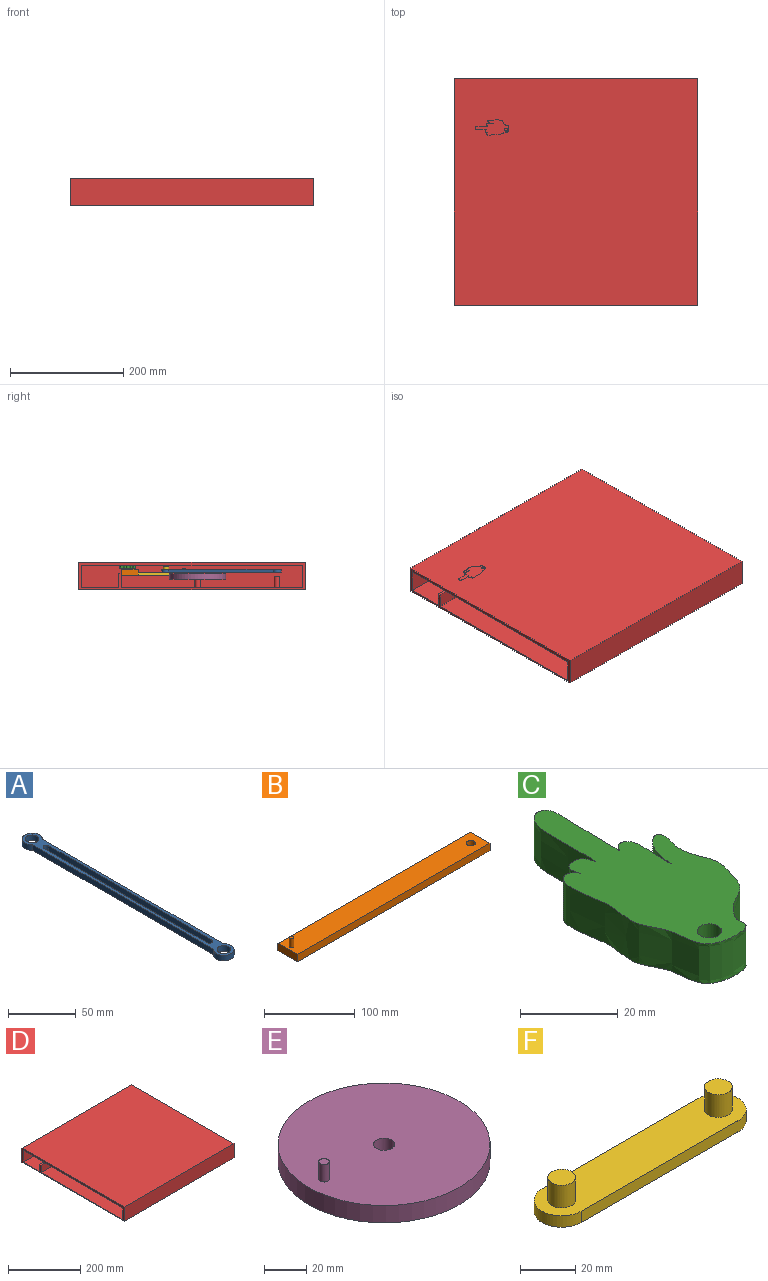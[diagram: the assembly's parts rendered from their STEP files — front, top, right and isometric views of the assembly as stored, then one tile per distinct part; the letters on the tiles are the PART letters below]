
ASSEMBLY  parts=6 mates=8
PART A: 12 faces, bbox 15x215x5 mm
  f0: plane 188.82x5mm, normal (1,0,0), area 944.1mm2, adj f1,f9,f10,f11
  f1: cylinder r=7.5mm len=15mm, axis (0,0,-1), area 180.9mm2, adj f0,f2,f10,f11
  f2: plane 188.82x5mm, normal (-1,0,0), area 944.1mm2, adj f1,f9,f10,f11
  f3: plane 170x5mm, normal (1,0,0), area 850mm2, adj f4,f6,f10,f11
  f4: cylinder r=2.5mm len=5mm, axis (0,0,-1), area 39.3mm2, adj f3,f5,f10,f11
  f5: plane 170x5mm, normal (-1,0,0), area 850mm2, adj f4,f6,f10,f11
  f6: cylinder r=2.5mm len=5mm, axis (0,0,-1), area 39.3mm2, adj f3,f5,f10,f11
  f7: cylinder r=5mm len=10mm, axis (0,0,-1), area 157.1mm2, adj f10,f11
  f8: cylinder r=5mm len=10mm, axis (0,0,-1), area 157.1mm2, adj f10,f11
  f9: cylinder r=7.5mm len=15mm, axis (0,0,-1), area 180.9mm2, adj f0,f2,f10,f11
  f10: plane 215x15mm, normal (0,0,1), area 1188.7mm2, adj f0,f1,f2,f3,f4,f5,f6,f7
  f11: plane 215x15mm, normal (0,0,-1), area 1188.7mm2, adj f0,f1,f2,f3,f4,f5,f6,f7
PART B: 9 faces, bbox 300x30x22.4 mm
  f0: plane 300x10mm, normal (0,1,0), area 3000mm2, adj f1,f4,f5,f6
  f1: plane 30x10mm, normal (-1,0,0), area 300mm2, adj f0,f2,f5,f6
  f2: plane 300x10mm, normal (0,-1,0), area 3000mm2, adj f1,f4,f5,f6
  f3: cylinder r=5mm len=10mm, axis (0,0,-1), area 314.2mm2, adj f5,f6
  f4: plane 30x10mm, normal (1,0,0), area 300mm2, adj f0,f2,f5,f6
  f5: plane 300x30mm, normal (0,0,1), area 8901.8mm2, adj f0,f1,f2,f3,f4,f7
  f6: plane 300x30mm, normal (0,0,-1), area 8921.5mm2, adj f0,f1,f2,f3,f4
  f7: cylinder r=2.5mm len=12.4mm, axis (0,0,-1), area 194.8mm2, adj f5,f8
  f8: plane 5x5mm, normal (0,0,1), area 19.6mm2, adj f7
PART C: 4 faces, bbox 28.3x60.6x10 mm
  f0: extruded ~58.81x27.04mm, area 1895.4mm2, adj f1,f2
  f1: plane 60.61x28.31mm, normal (0,0,1), area 962.1mm2, adj f0,f3
  f2: plane 60.61x28.31mm, normal (0,0,-1), area 962.1mm2, adj f0,f3
  f3: cylinder r=2.5mm len=10mm, axis (0,0,1), area 157.1mm2, adj f1,f2
PART D: 19 faces, bbox 430x400x48 mm
  f0: plane 425x390mm, normal (0,0,1), area 164592.9mm2, adj f2,f6,f8,f10,f11,f12,f14,f15
  f1: plane 430x48mm, normal (0,1,0), area 20640mm2, adj f2,f4,f5,f18
  f2: plane 400x48mm, normal (-1,0,0), area 3725mm2, adj f0,f1,f3,f5,f10,f11,f13,f14
  f3: plane 430x48mm, normal (0,-1,0), area 20640mm2, adj f2,f4,f5,f18
  f4: plane 400x48mm, normal (1,0,0), area 19200mm2, adj f1,f3,f5,f18
  f5: plane 430x400mm, normal (0,0,-1), area 172000mm2, adj f1,f2,f3,f4
  f6: cylinder r=5mm len=20mm, axis (0,0,-1), area 628.3mm2, adj f0,f7
  f7: plane 10x10mm, normal (0,0,1), area 78.5mm2, adj f6
  f8: cylinder r=5mm len=20mm, axis (0,0,-1), area 628.3mm2, adj f0,f9
  f9: plane 10x10mm, normal (0,0,1), area 78.5mm2, adj f8
  f10: plane 200x25mm, normal (0,1,0), area 5000mm2, adj f0,f2,f12,f13
  f11: plane 200x25mm, normal (0,-1,0), area 5000mm2, adj f0,f2,f12,f13
  f12: plane 25x5mm, normal (1,0,0), area 125mm2, adj f0,f10,f11,f13
  f13: plane 200x5mm, normal (0,0,1), area 1000mm2, adj f2,f10,f11,f12
  f14: plane 425x40mm, normal (0,-1,0), area 17000mm2, adj f0,f2,f15,f17
  f15: plane 390x40mm, normal (-1,0,0), area 15600mm2, adj f0,f14,f16,f17
  f16: plane 425x40mm, normal (0,1,0), area 17000mm2, adj f0,f2,f15,f17
  f17: plane 425x390mm, normal (0,0,-1), area 165750mm2, adj f2,f14,f15,f16
  f18: plane 430x400mm, normal (0,0,1), area 172000mm2, adj f1,f2,f3,f4
PART E: 6 faces, bbox 100x100x20 mm
  f0: cylinder r=5mm len=10mm, axis (0,0,-1), area 314.2mm2, adj f2,f3
  f1: cylinder r=50mm len=100mm, axis (0,0,-1), area 3141.6mm2, adj f2,f3
  f2: plane 100x100mm, normal (0,0,1), area 7755.8mm2, adj f0,f1,f4
  f3: plane 100x100mm, normal (0,0,-1), area 7775.4mm2, adj f0,f1
  f4: cylinder r=2.5mm len=10mm, axis (0,0,-1), area 157.1mm2, adj f2,f5
  f5: plane 5x5mm, normal (0,0,1), area 19.6mm2, adj f4
PART F: 10 faces, bbox 100x20x15 mm
  f0: plane 80x5mm, normal (0,1,0), area 400mm2, adj f1,f3,f4,f5
  f1: cylinder r=10mm len=20mm, axis (0,0,-1), area 157.1mm2, adj f0,f2,f4,f5
  f2: plane 80x5mm, normal (0,-1,0), area 400mm2, adj f1,f3,f4,f5
  f3: cylinder r=10mm len=20mm, axis (0,0,-1), area 157.1mm2, adj f0,f2,f4,f5
  f4: plane 100x20mm, normal (0,0,1), area 1757.1mm2, adj f0,f1,f2,f3,f6,f8
  f5: plane 100x20mm, normal (0,0,-1), area 1914.2mm2, adj f0,f1,f2,f3
  f6: cylinder r=5mm len=10mm, axis (0,0,-1), area 314.2mm2, adj f4,f7
  f7: plane 10x10mm, normal (0,0,1), area 78.5mm2, adj f6
  f8: cylinder r=5mm len=10mm, axis (0,0,-1), area 314.2mm2, adj f4,f9
  f9: plane 10x10mm, normal (0,0,1), area 78.5mm2, adj f8
PLACE A rot(axis=(0,0,-1),11.1deg) t=(94.62,-59.2,34.76)mm
PLACE B t=(-69.41,102.68,29.76)mm
PLACE C rot(axis=(0,0,1),91.2deg) t=(-191.16,140.02,42.16)mm
PLACE D t=(-89.67,-7.32,4.26)mm fixed
PLACE E rot(axis=(0,0,-1),143.6deg) t=(75.33,-17.32,22.26)mm
PLACE F rot(axis=(0,0,-1),52.8deg) t=(89.76,70.8,29.76)mm
MATE pin_slot E.f4 <-> A.f4  axis (0,0,-1) through (107.53,6.42,37.26)mm
MATE revolute A.f7 <-> D.f6  axis (0,0,-1) through (75.33,-157.32,37.26)mm
MATE revolute F.f6 <-> B.f3  axis (0,0,-1) through (65.59,102.68,39.76)mm
MATE planar B.f0 <-> D.f11  axis (0,1,0) through (-69.41,117.68,34.76)mm
MATE revolute F.f8 <-> A.f8  axis (0,0,-1) through (113.92,38.92,39.76)mm
MATE revolute C.f3 <-> B.f7  axis (0,0,1) through (-213.21,102.68,52.16)mm
MATE parallel B.f0 <-> D.f1  axis (0,1,0) through (-69.41,117.68,34.76)mm
MATE revolute E.f0 <-> D.f8  axis (0,0,-1) through (75.33,-17.32,27.26)mm
